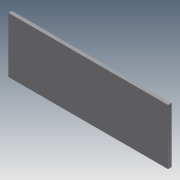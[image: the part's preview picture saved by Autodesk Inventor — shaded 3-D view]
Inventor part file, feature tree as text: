
AUTODESK INVENTOR PART (.ipt)
format: ipt  version: 2011 (Build 150239000, 239)  size: 123,904 bytes
history: native  units: in
note: dims shown in document units (in); Inventor stores cm internally (conversion verified against a paired STEP export)
features: extrude x5, sketch x5
ambient origin geometry x8: Origin, YZ Plane, XZ Plane, XY Plane, X Axis, Y Axis, Z Axis, Center Point
bodies: Solid1 (feature_tree)
feature tree (10):
  extrude  "Extrusion1"  Depth=4.0in
  extrude  "Extrusion2"  Depth=0.25in
  extrude  "Extrusion3"  Depth=0.25in
  extrude  "Extrusion4"  Depth=1.0in TaperAngle=0.0deg
  extrude  "Extrusion5"  Depth=0.25in
  sketch  "Sketch1"  dims[d0=11.5in d1=4.0in]
  sketch  "Sketch2"  dims[d2=0.25in d3=0.0in d4=0.25in]
  sketch  "Sketch3"  dims[d5=0.6in d6=0.25in]
  sketch  "Sketch4"  dims[d7=0.6in d8=1.0in d9=0.0in]
  sketch  "Sketch5"  dims[d10=0.25in d11=0.25in d12=0.25in d13=0.0in d14=1.375in d15=3.858in d16=7.75in d17=0.1875in d18=0.25in d19=0.0in d20=0.25in d21=0.0in]
